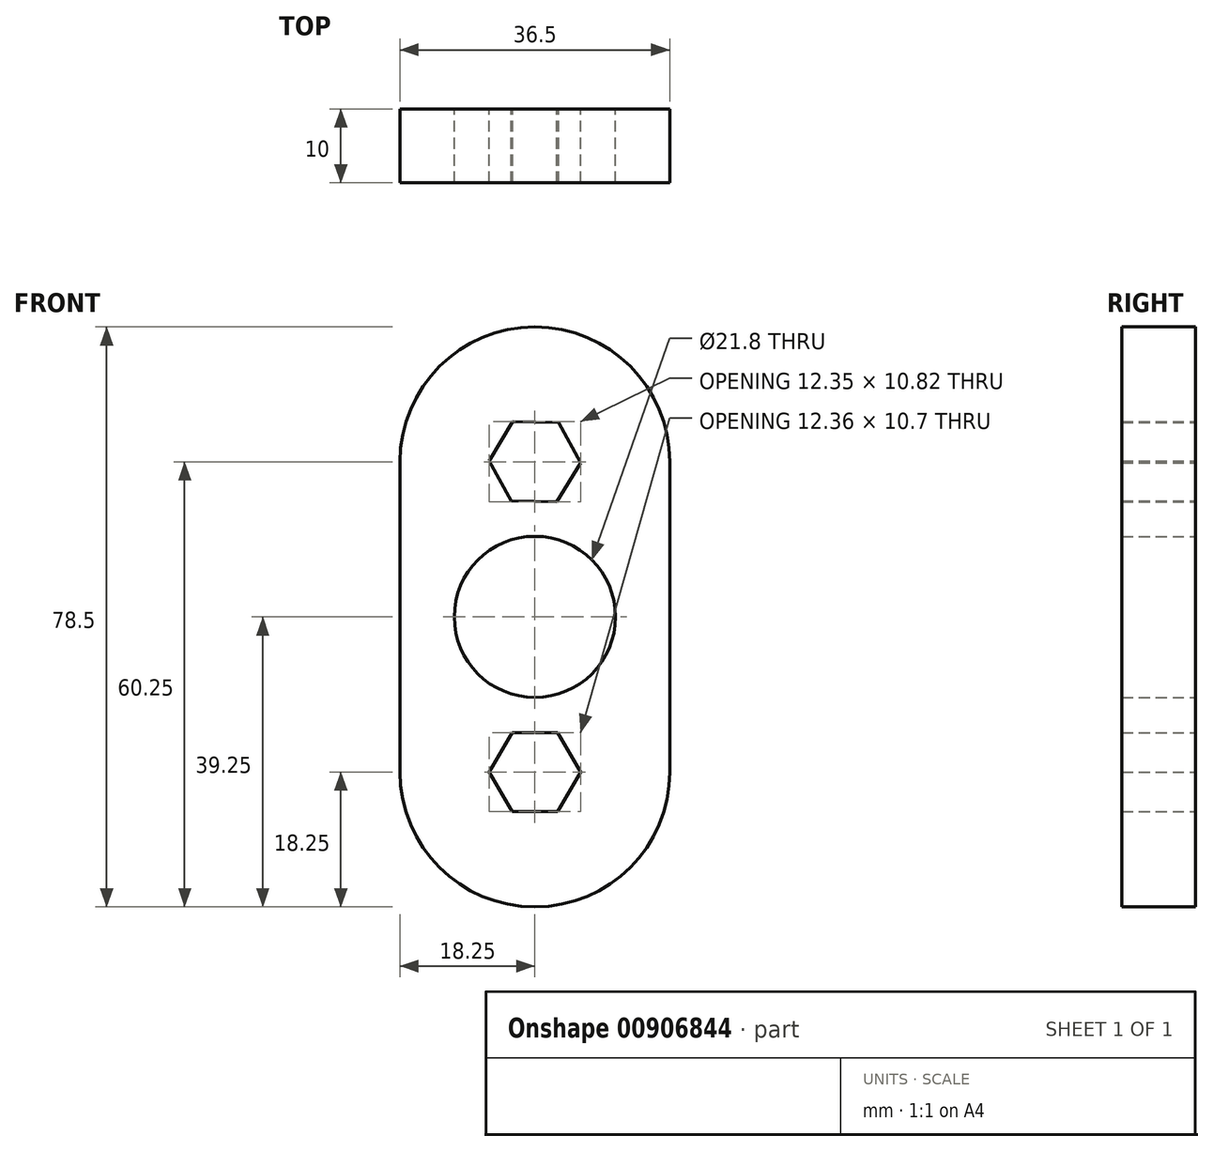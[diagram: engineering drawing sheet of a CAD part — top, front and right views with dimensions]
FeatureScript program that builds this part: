
annotation { "Feature Type Name" : "Feature", "Feature Type Description" : "" }
export const myFeature = defineFeature(function(context is Context, id is Id, definition is map)
    precondition{}
    {
        {
            var Q0;
            Q0=qCreatedBy(makeId("Front.planeOp"),FACE);
            var sketch = newSketch(context, id + "F0", { "sketchPlane" : qUnion([Q0])});
            skCircle(sketch, "E0", {"center": v(0, 0) * mm, "radius": 10.9 * mm});
            skLineSegment(sketch, "E1", {"start": v(-18.25, -21) * mm, "end": v(-18.25, 21) * mm});
            skLineSegment(sketch, "E2", {"start": v(18.25, 21) * mm, "end": v(18.25, -21) * mm});
            skArc(sketch, "E3", {"start": v(18.25, 21) * mm, "mid": v(0, 39.25) * mm, "end": v(-18.25, 21) * mm});
            skArc(sketch, "E4", {"start": v(-18.25, -21) * mm, "mid": v(0, -39.25) * mm, "end": v(18.25, -21) * mm});
            skCircle(sketch, "E5.cCircle", {"center": v(0, 21) * mm, "radius": 5.35 * mm, "construction": true});
            skLineSegment(sketch, "E5.0", {"start": v(3.2, 26.29) * mm, "end": v(6.18, 20.87) * mm});
            skLineSegment(sketch, "E5.1", {"start": v(6.18, 20.87) * mm, "end": v(2.98, 15.59) * mm});
            skLineSegment(sketch, "E5.2", {"start": v(2.98, 15.59) * mm, "end": v(-3.2, 15.71) * mm});
            skLineSegment(sketch, "E5.3", {"start": v(-3.2, 15.71) * mm, "end": v(-6.18, 21.13) * mm});
            skLineSegment(sketch, "E5.4", {"start": v(-6.18, 21.13) * mm, "end": v(-2.98, 26.41) * mm});
            skLineSegment(sketch, "E5.5", {"start": v(-2.98, 26.41) * mm, "end": v(3.2, 26.29) * mm});
            skPoint(sketch, "E5.0.midPoint", {"position": v(4.69, 23.58) * mm});
            skCircle(sketch, "E6.cCircle", {"center": v(0, -21) * mm, "radius": 5.35 * mm, "construction": true});
            skLineSegment(sketch, "E6.0", {"start": v(-3.09, -15.65) * mm, "end": v(3.09, -15.65) * mm});
            skLineSegment(sketch, "E6.1", {"start": v(3.09, -15.65) * mm, "end": v(6.18, -21) * mm});
            skLineSegment(sketch, "E6.2", {"start": v(6.18, -21) * mm, "end": v(3.09, -26.35) * mm});
            skLineSegment(sketch, "E6.3", {"start": v(3.09, -26.35) * mm, "end": v(-3.09, -26.35) * mm});
            skLineSegment(sketch, "E6.4", {"start": v(-3.09, -26.35) * mm, "end": v(-6.18, -21) * mm});
            skLineSegment(sketch, "E6.5", {"start": v(-6.18, -21) * mm, "end": v(-3.09, -15.65) * mm});
            skPoint(sketch, "E6.0.midPoint", {"position": v(0, -15.65) * mm});
            skSolve(sketch);
        }
        {
            var Q0;
            Q0 = qSketchRegion(id + "F0", true);
            extrude(context, id + "F1", {"entities" : qUnion([Q0]), "depth" : 10 * mm, "offsetDistance" : 25 * mm});
        }
    });
